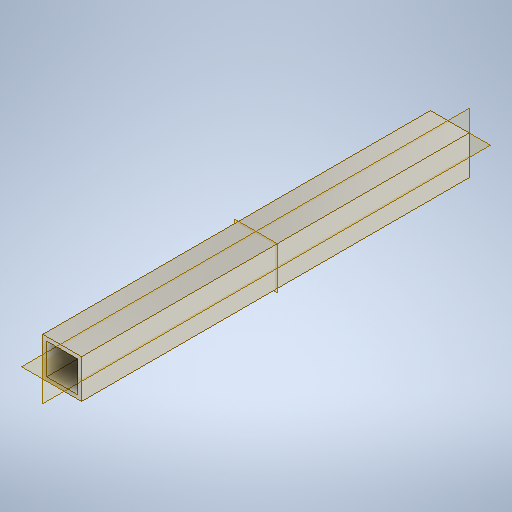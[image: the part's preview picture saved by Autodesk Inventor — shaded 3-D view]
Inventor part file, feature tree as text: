
AUTODESK INVENTOR PART (.ipt)
format: ipt  version: 2025.2 (Build 292293000, 293)  size: 231,936 bytes
history: native  units: mm
features: other x1, extrude x1, sketch x1
ambient origin geometry x8: Origin, YZ Plane, XZ Plane, XY Plane, X Axis, Y Axis, Z Axis, Center Point
bodies: Body1 (feature_tree)
feature tree (3):
  other  "Sólido1"
  extrude  "Extrusão1"  Depth=2.0mm
  sketch  "Esboço1"  dims[d0=20.0mm d1=2.0mm d2=200.0mm d3=0.0mm]
